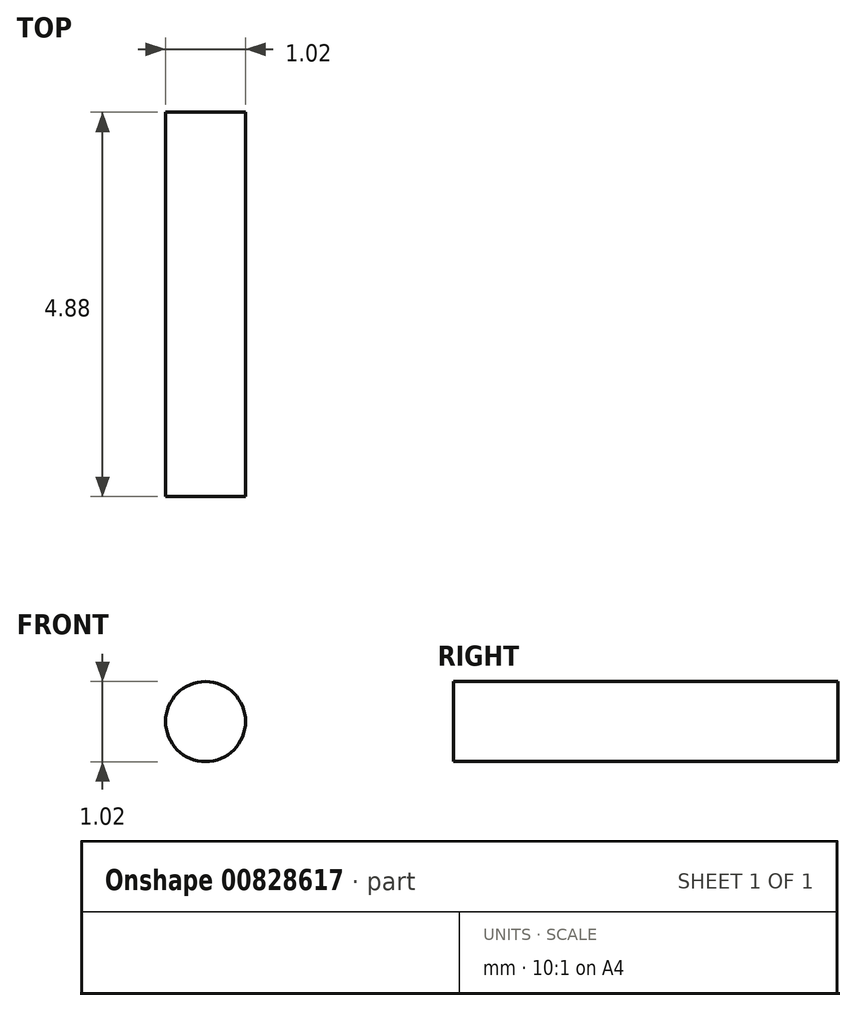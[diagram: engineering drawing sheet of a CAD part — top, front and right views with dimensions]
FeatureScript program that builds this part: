
annotation { "Feature Type Name" : "Feature", "Feature Type Description" : "" }
export const myFeature = defineFeature(function(context is Context, id is Id, definition is map)
    precondition{}
    {
        {
            var Q0;
            Q0=qCreatedBy(makeId("Front.planeOp"),FACE);
            var sketch = newSketch(context, id + "F0", { "sketchPlane" : qUnion([Q0])});
            skCircle(sketch, "E0", {"center": v(0, 0) * mm, "radius": 0.5 * mm});
            skSolve(sketch);
        }
        {
            var Q0;
            Q0 = qSketchRegion(id + "F0", true);
            extrude(context, id + "F1", {"entities" : qUnion([Q0]), "endBound" : BoundingType.SYMMETRIC, "depth" : 4.88 * mm, "offsetDistance" : 25.4 * mm});
        }
    });
